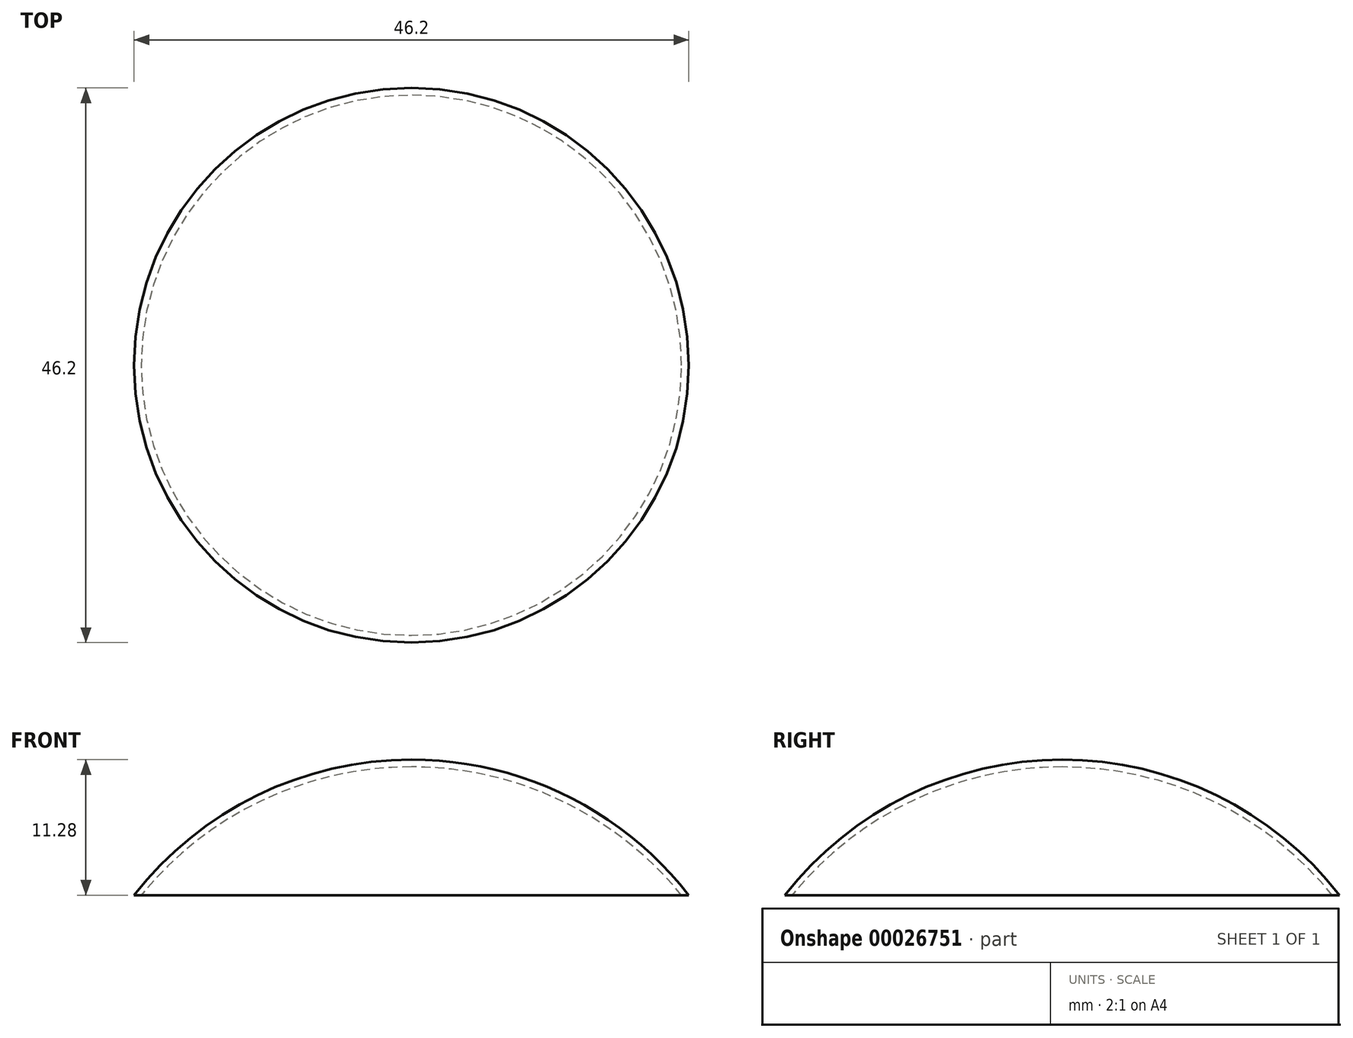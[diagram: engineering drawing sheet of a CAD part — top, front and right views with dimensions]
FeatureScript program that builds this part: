
annotation { "Feature Type Name" : "Feature", "Feature Type Description" : "" }
export const myFeature = defineFeature(function(context is Context, id is Id, definition is map)
    precondition{}
    {
        {
            var Q0;
            Q0=qCreatedBy(makeId("Front.planeOp"),FACE);
            var sketch = newSketch(context, id + "F0", { "sketchPlane" : qUnion([Q0])});
            skArc(sketch, "E0", {"start": v(22.5, 0) * mm, "mid": v(12.45, 7.87) * mm, "end": v(0, 10.68) * mm});
            skLineSegment(sketch, "E1", {"start": v(0, 10.68) * mm, "end": v(0, 11.28) * mm});
            skLineSegment(sketch, "E2", {"start": v(22.5, 0) * mm, "end": v(23.1, 0) * mm});
            skArc(sketch, "E3", {"start": v(23.1, 0) * mm, "mid": v(12.85, 8.3) * mm, "end": v(0, 11.28) * mm});
            skSolve(sketch);
        }
        {
            var Q0;
            Q0=qCreatedBy(makeId("Front.planeOp"),FACE);
            var sketch = newSketch(context, id + "F1", { "sketchPlane" : qUnion([Q0])});
            skLineSegment(sketch, "E4", {"start": v(0, 34.82) * mm, "end": v(0, -31.4) * mm, "construction": true});
            skSolve(sketch);
        }
        {
            var Q0;
            Q0=makeQuery(id+"F0.imprint","IMPRINT",FACE,{"disambiguationData":[TD([[makeQuery(id+"F0.imprint","IMPRINT",EDGE,{"derivedFrom":sQuery(id+"F0.wireOp",EDGE,"E0")}),-1.0]])]});
            var Q1;
            Q1=sQuery(id+"F1.wireOp",EDGE,"E4");
            revolve(context, id + "F2", {"entities" : qUnion([Q0]), "axis" : qUnion([Q1]), "revolveType" : RevolveType.FULL});
        }
    });
